# Revit family: LQ4010001_Regadera con Brazo Liquid
name_source: partatom
category: Plumbing Fixtures
units: mm (PartAtom-declared; Revit-internal decimal feet)

## family parameters
Always vertical = Yes
Cut with Voids When Loaded = No
Host = Wall
OmniClass Number = 23.31.15.11
OmniClass Title = Bath Shower Units
Part Type = Normal
Room Calculation Point = No
Round Connector Dimension = Use Diameter
Shared = No

## types (1)
- Type 1
    Alto = 16.5 cm
    Altura ducha = 1800 mm  [stored 5.90551 ft]
    Ancho = 24.1 cm
    Capacidad de flujo = 9.50 l/m máximo a 80 psi
    Colección = Liquid
    Consumo de agua = 9.5 lt
    Creado por = IDD
    Description = Pide hoy mismo la regadera Liquid. Con tecnología de ahorro de agua que minimiza el derroche, ofreciendo un mayor rendimiento sin sacrificar el confort en la ducha. Disfruta de una relajación completa.
    Dimensión de la regadera = 24.1
    Fecha de creación = 21/07/2020
    Forma = Redondo
    Garantía = 30 años en estructura
    Garantías de otros componentes = 5 años en acabados
    Incluye = Regadera, brazo de la regadera
    Largo = 41.5 cm
    Longitud del brazo = 41.5
    Línea = Liquid
    Material = Corona_Plastico_Cromado
    Materiales = Polímero de alta ingeniería, Metal
    Productos compatibles = Mezcladores 8 pulgadas, mezcladores monocontrol con desviador, mezcladores monocontrol sin desviador, registros para ducha
    Rango de presión de agua = Entre 20 y 125 psi
    Resistencia = Resistente a la corrosión pelado y decoloración por agua
    Tecnología = DuraCrome
    Tecnologías = EcoStream
    Temperatura de uso = Entre 5˚C y 71˚C
    Tipo de chorro = Tipo lluvia
    Tipo de grifería = Monocontrol
    Tipo de manija/accionamiento = Palanca
    Tipo de regadera = Diámetro amplio, regadera con brazo
    URL = https://corona.co
    Uso = Residencial

note: [stored X ft] marks values corroborated as IEEE doubles in the binary element streams (Revit-internal decimal feet)

## geometry (parser evidence)
native form markers: Sweep x11
no freeform markers — native parametric forms only
